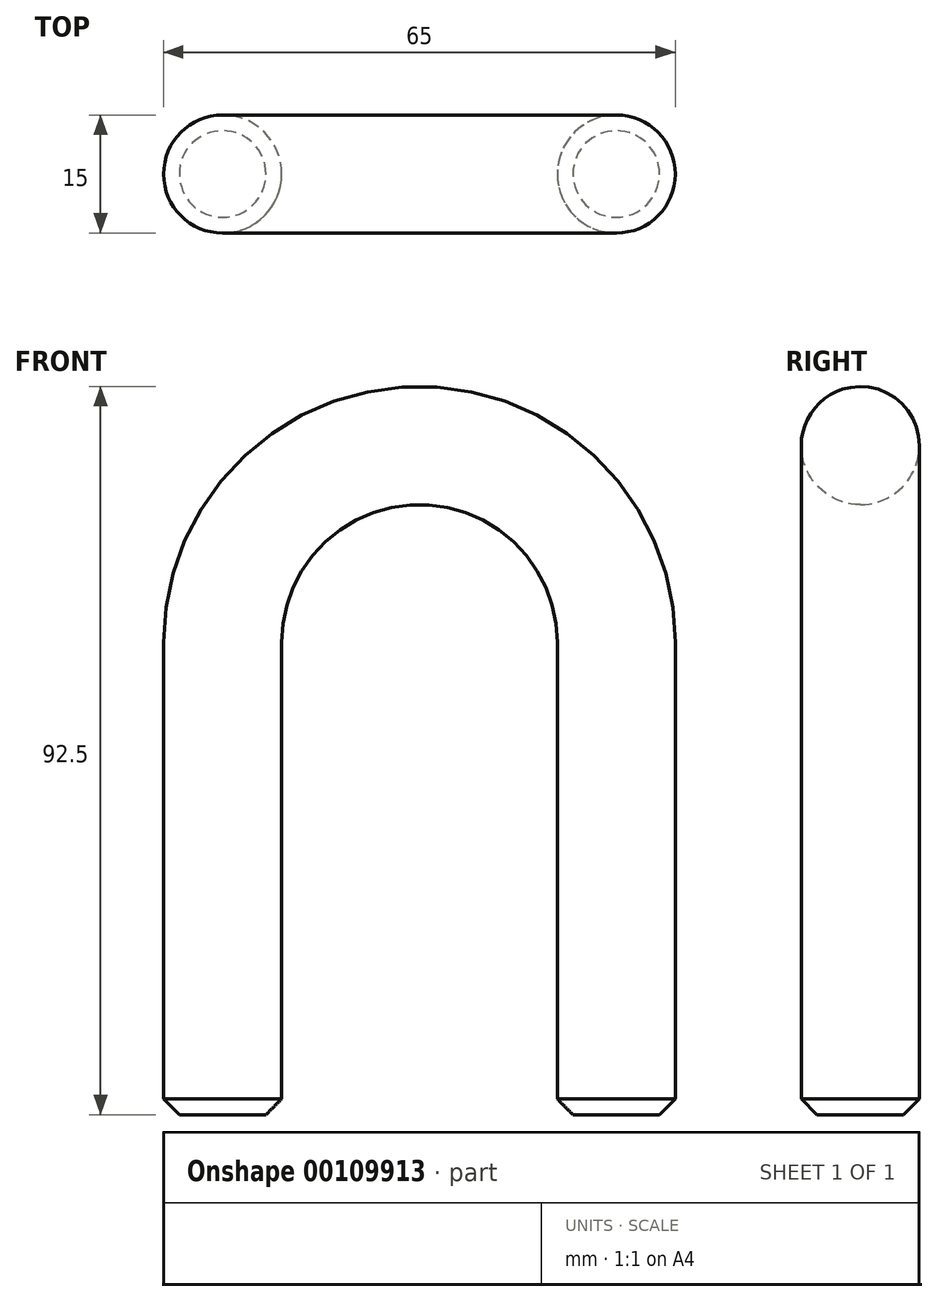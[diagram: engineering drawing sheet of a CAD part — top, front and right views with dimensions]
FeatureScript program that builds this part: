
annotation { "Feature Type Name" : "Feature", "Feature Type Description" : "" }
export const myFeature = defineFeature(function(context is Context, id is Id, definition is map)
    precondition{}
    {
        {
            var Q0;
            Q0=qCreatedBy(makeId("Front.planeOp"),FACE);
            var sketch = newSketch(context, id + "F0", { "sketchPlane" : qUnion([Q0])});
            skLineSegment(sketch, "E0", {"start": v(0, 0) * mm, "end": v(0, 60) * mm});
            skArc(sketch, "E1", {"start": v(50, 60) * mm, "mid": v(25, 85) * mm, "end": v(0, 60) * mm});
            skLineSegment(sketch, "E2", {"start": v(50, 60) * mm, "end": v(50, 0) * mm});
            skSolve(sketch);
        }
        {
            var Q0;
            Q0=qCreatedBy(makeId("Top.planeOp"),FACE);
            var sketch = newSketch(context, id + "F1", { "sketchPlane" : qUnion([Q0])});
            skCircle(sketch, "E3", {"center": v(0, 0) * mm, "radius": 7.5 * mm});
            skSolve(sketch);
        }
        {
            var Q0;
            Q0=makeQuery(id+"F1.imprint","IMPRINT",FACE,{"disambiguationData":[TD([[makeQuery(id+"F1.imprint","IMPRINT",EDGE,{"derivedFrom":sQuery(id+"F1.wireOp",EDGE,"E3")}),1.0]])]});
            var Q1;
            Q1=sQuery(id+"F0.wireOp",EDGE,"E0");
            var Q2;
            Q2=sQuery(id+"F0.wireOp",EDGE,"E1");
            var Q3;
            Q3=sQuery(id+"F0.wireOp",EDGE,"E2");
            sweep(context, id + "F2", {"profiles" : qUnion([Q0]), "path" : qUnion([Q1, Q2, Q3])});
        }
        {
            var Q0;
            Q0=makeQuery(id+"F2.opSweep","CAP_EDGE",EDGE,{"disambiguationData":[OSD([sQuery(id+"F0.wireOp",VERTEX,"E0.start"),sQuery(id+"F1.wireOp",EDGE,"E3")])],"isStart":true});
            var Q1;
            Q1=makeQuery(id+"F2.opSweep","CAP_EDGE",EDGE,{"disambiguationData":[OSD([sQuery(id+"F0.wireOp",VERTEX,"E2.end"),sQuery(id+"F1.wireOp",EDGE,"E3")])],"isStart":false});
            chamfer(context, id + "F3", {"entities" : qUnion([Q0, Q1]), "width" : 2 * mm, "tangentPropagation" : true});
        }
    });
